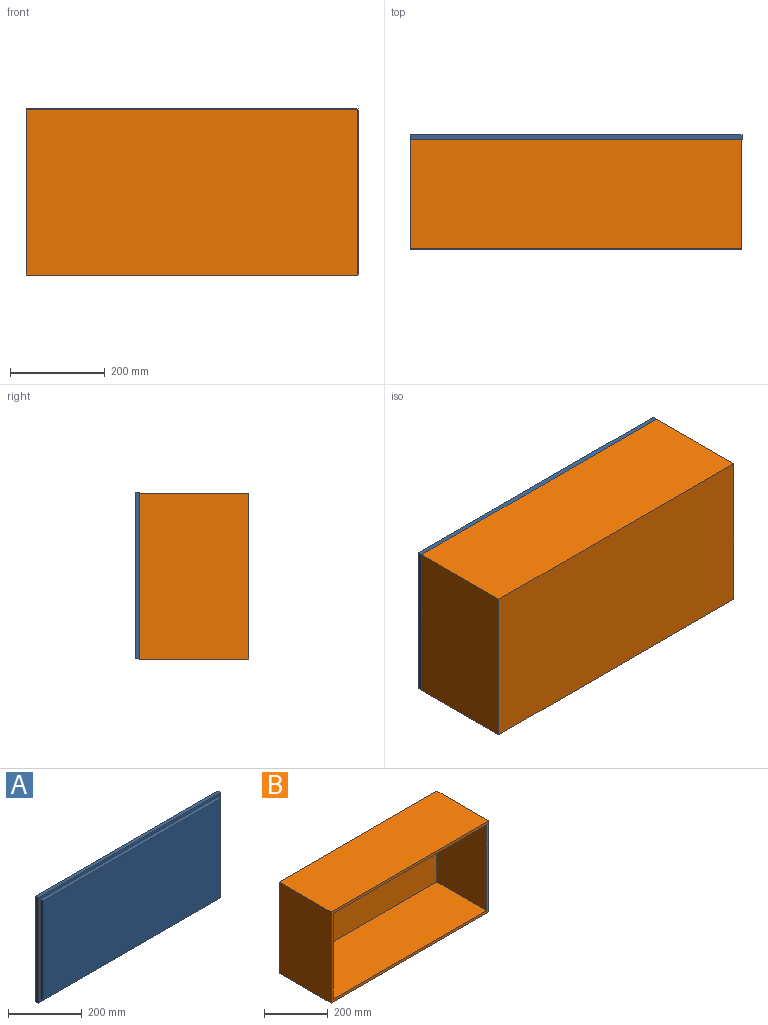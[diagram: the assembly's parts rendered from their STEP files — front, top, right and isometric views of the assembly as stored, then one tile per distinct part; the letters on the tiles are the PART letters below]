
ASSEMBLY  parts=2 mates=1
PART A: 11 faces, bbox 700x20x350 mm
  f0: plane 700x10mm, normal (0,0,1), area 7000mm2, adj f1,f3,f4,f5
  f1: plane 350x10mm, normal (-1,0,0), area 3500mm2, adj f0,f2,f4,f5
  f2: plane 700x10mm, normal (0,0,-1), area 7000mm2, adj f1,f3,f4,f5
  f3: plane 350x10mm, normal (1,0,0), area 3500mm2, adj f0,f2,f4,f5
  f4: plane 700x350mm, normal (0,-1,0), area 20600mm2, adj f0,f1,f2,f3,f6,f7,f8,f9
  f5: plane 700x350mm, normal (0,1,0), area 245000mm2, adj f0,f1,f2,f3
  f6: plane 680x10mm, normal (0,0,1), area 6800mm2, adj f4,f7,f9,f10
  f7: plane 330x10mm, normal (-1,0,0), area 3300mm2, adj f4,f6,f8,f10
  f8: plane 680x10mm, normal (0,0,-1), area 6800mm2, adj f4,f7,f9,f10
  f9: plane 330x10mm, normal (1,0,0), area 3300mm2, adj f4,f6,f8,f10
  f10: plane 680x330mm, normal (0,-1,0), area 224400mm2, adj f6,f7,f8,f9
PART B: 11 faces, bbox 700x230x350 mm
  f0: plane 700x350mm, normal (0,-1,0), area 20600mm2, adj f1,f2,f3,f4,f6,f7,f8,f9
  f1: plane 700x230mm, normal (0,0,1), area 161000mm2, adj f0,f2,f4,f5
  f2: plane 350x230mm, normal (-1,0,0), area 80500mm2, adj f0,f1,f3,f5
  f3: plane 700x230mm, normal (0,0,-1), area 161000mm2, adj f0,f2,f4,f5
  f4: plane 350x230mm, normal (1,0,0), area 80500mm2, adj f0,f1,f3,f5
  f5: plane 700x350mm, normal (0,1,0), area 245000mm2, adj f1,f2,f3,f4
  f6: plane 680x220mm, normal (0,0,-1), area 149600mm2, adj f0,f7,f9,f10
  f7: plane 330x220mm, normal (1,0,0), area 72600mm2, adj f0,f6,f8,f10
  f8: plane 680x220mm, normal (0,0,1), area 149600mm2, adj f0,f7,f9,f10
  f9: plane 330x220mm, normal (-1,0,0), area 72600mm2, adj f0,f6,f8,f10
  f10: plane 680x330mm, normal (0,-1,0), area 224400mm2, adj f6,f7,f8,f9
PLACE A t=(-574.63,-169.72,-179.25)mm
PLACE B rot(axis=(-1,0,0),180deg) t=(-573.39,-409.72,-325.89)mm
MATE fastened A.f4 <-> B.f0  axis (0,-1,0) through (-223.39,-179.72,-325.89)mm
